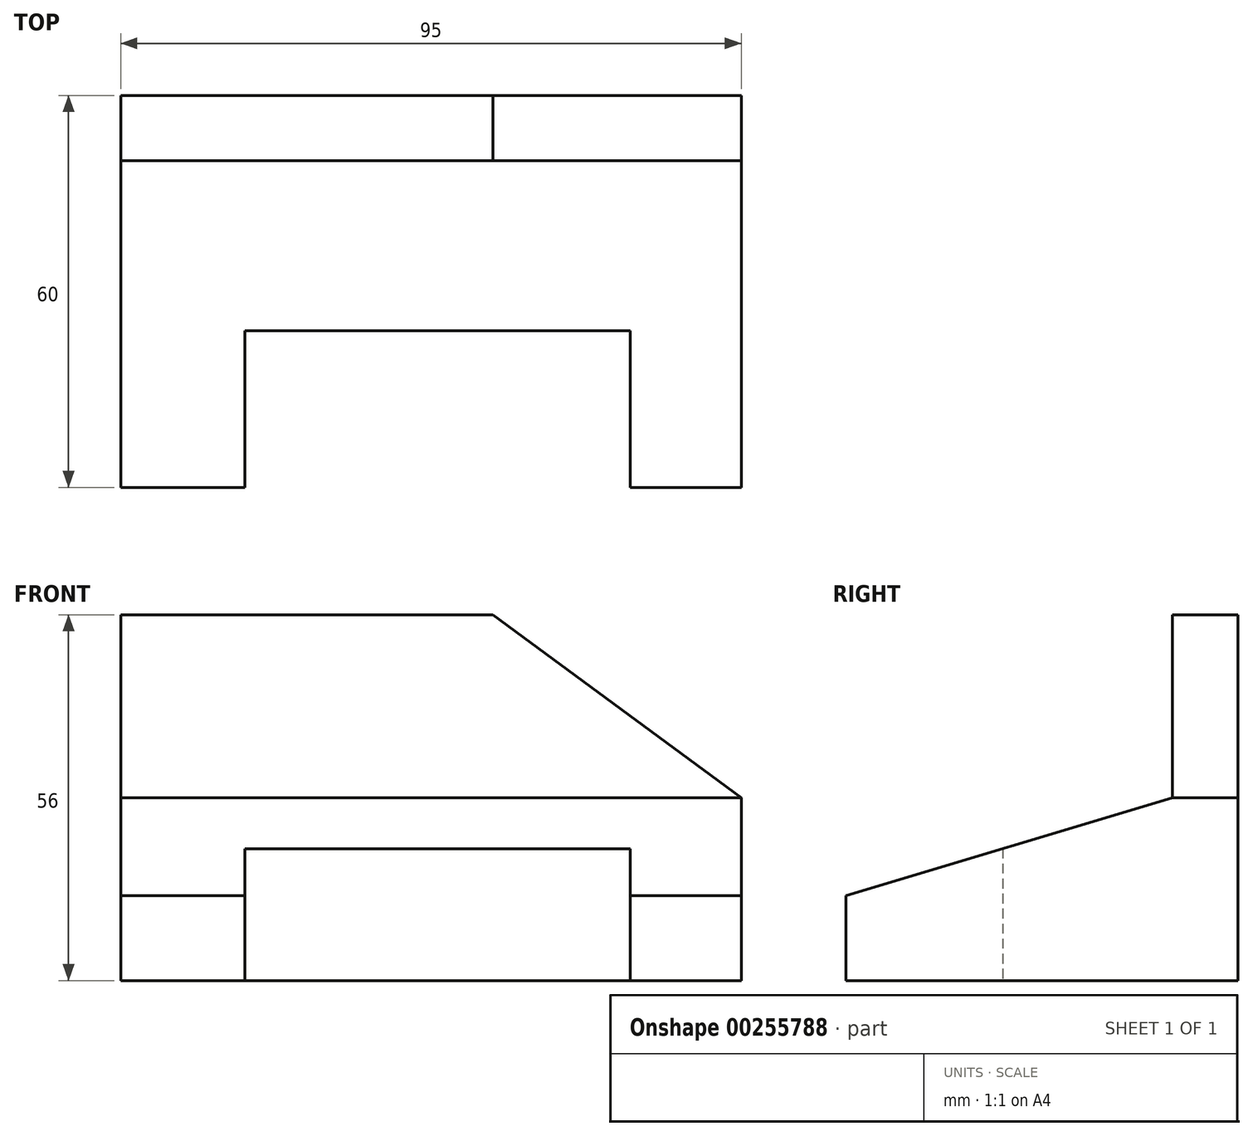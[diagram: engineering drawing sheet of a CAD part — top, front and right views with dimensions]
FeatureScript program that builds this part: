
annotation { "Feature Type Name" : "Feature", "Feature Type Description" : "" }
export const myFeature = defineFeature(function(context is Context, id is Id, definition is map)
    precondition{}
    {
        {
            var Q0;
            Q0=qCreatedBy(makeId("Right.planeOp"),FACE);
            var sketch = newSketch(context, id + "F0", { "sketchPlane" : qUnion([Q0])});
            skLineSegment(sketch, "E0", {"start": v(0, 0) * mm, "end": v(-60, 0) * mm});
            skLineSegment(sketch, "E1", {"start": v(-60, 0) * mm, "end": v(-60, 13) * mm});
            skLineSegment(sketch, "E2", {"start": v(-60, 13) * mm, "end": v(-10, 28) * mm});
            skLineSegment(sketch, "E3", {"start": v(-10, 28) * mm, "end": v(-10, 56) * mm});
            skLineSegment(sketch, "E4", {"start": v(-10, 56) * mm, "end": v(0, 56) * mm});
            skLineSegment(sketch, "E5", {"start": v(0, 56) * mm, "end": v(0, 0) * mm});
            skSolve(sketch);
        }
        {
            var Q0;
            Q0=makeQuery(id+"F0.imprint","IMPRINT",FACE,{"disambiguationData":[TD([[makeQuery(id+"F0.imprint","IMPRINT",EDGE,{"derivedFrom":sQuery(id+"F0.wireOp",EDGE,"E0")}),-1.0]])]});
            extrude(context, id + "F1", {"entities" : qUnion([Q0]), "depth" : 95 * mm});
        }
        {
            var Q0;
            Q0=makeQuery(id+"F1.opExtrude","SWEPT_FACE",FACE,{"disambiguationData":[OSD([sQuery(id+"F0.wireOp",EDGE,"E3")])]});
            var sketch = newSketch(context, id + "F2", { "sketchPlane" : qUnion([Q0])});
            skLineSegment(sketch, "E6", {"start": v(57, 56) * mm, "end": v(95, 28) * mm});
            skSolve(sketch);
        }
        {
            var Q0;
            {var subQ0=sQuery(id+"F2.wireOp",EDGE,"E6");Q0=makeQuery(id+"F2.imprint","IMPRINT",FACE,{"disambiguationData":[TD([[makeQuery(id+"F2.imprint","IMPRINT",EDGE,{"derivedFrom":subQ0}),1.0]])]});}
            extrude(context, id + "F3", {"entities" : qUnion([Q0]), "operationType" : NewBodyOperationType.REMOVE, "endBound" : BoundingType.THROUGH_ALL, "oppositeDirection" : true, "depth" : 25 * mm});
        }
        {
            var Q0;
            Q0=makeQuery(id+"F1.opExtrude","SWEPT_FACE",FACE,{"disambiguationData":[OSD([sQuery(id+"F0.wireOp",EDGE,"E0")])]});
            var sketch = newSketch(context, id + "F4", { "sketchPlane" : qUnion([Q0])});
            skLineSegment(sketch, "E7.bottom", {"start": v(19, 60) * mm, "end": v(78, 60) * mm});
            skLineSegment(sketch, "E7.top", {"start": v(19, 36) * mm, "end": v(78, 36) * mm});
            skLineSegment(sketch, "E7.left", {"start": v(19, 60) * mm, "end": v(19, 36) * mm});
            skLineSegment(sketch, "E7.right", {"start": v(78, 60) * mm, "end": v(78, 36) * mm});
            skSolve(sketch);
        }
        {
            var Q0;
            Q0=makeQuery(id+"F4.imprint","IMPRINT",FACE,{"disambiguationData":[TD([[makeQuery(id+"F4.imprint","IMPRINT",EDGE,{"derivedFrom":sQuery(id+"F4.wireOp",EDGE,"E7.bottom")}),1.0]])]});
            extrude(context, id + "F5", {"entities" : qUnion([Q0]), "operationType" : NewBodyOperationType.REMOVE, "endBound" : BoundingType.THROUGH_ALL, "oppositeDirection" : true, "depth" : 25 * mm});
        }
    });
